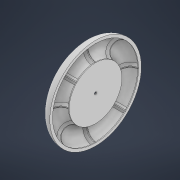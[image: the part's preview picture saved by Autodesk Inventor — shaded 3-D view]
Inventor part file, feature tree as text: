
AUTODESK INVENTOR PART (.ipt)
format: ipt  version: 2021 (Build 250183000, 183)  size: 712,704 bytes
history: native  units: mm
features: sketch x5, extrude x3, revolve x2, other x1, chamfer x1
ambient origin geometry x8: Origin, YZ Plane, XZ Plane, XY Plane, X Axis, Y Axis, Z Axis, Center Point
bodies: Body1 (feature_tree)
feature tree (12):
  other  "Твердое тело1"
  revolve  "Вращение1"
  extrude  "Выдавливание1"  TaperAngle=90.0deg  [1 undecoded]
  extrude  "Выдавливание2"  Depth=80.0mm TaperAngle=360.0deg
  revolve  "Вращение2"
  extrude  "Выдавливание3"  TaperAngle=0.0deg  [1 undecoded]
  chamfer  "Фаска1"  Distance=1.5mm
  sketch  "Эскиз1"
  sketch  "Эскиз2"
  sketch  "Эскиз3"
  sketch  "Эскиз4"
  sketch  "Эскиз5"
note: 2 required parameter values undecoded (feature->parameter linkage not recoverable at this tier; creation-order binding heuristic only, values carry confidence <= 0.55)
